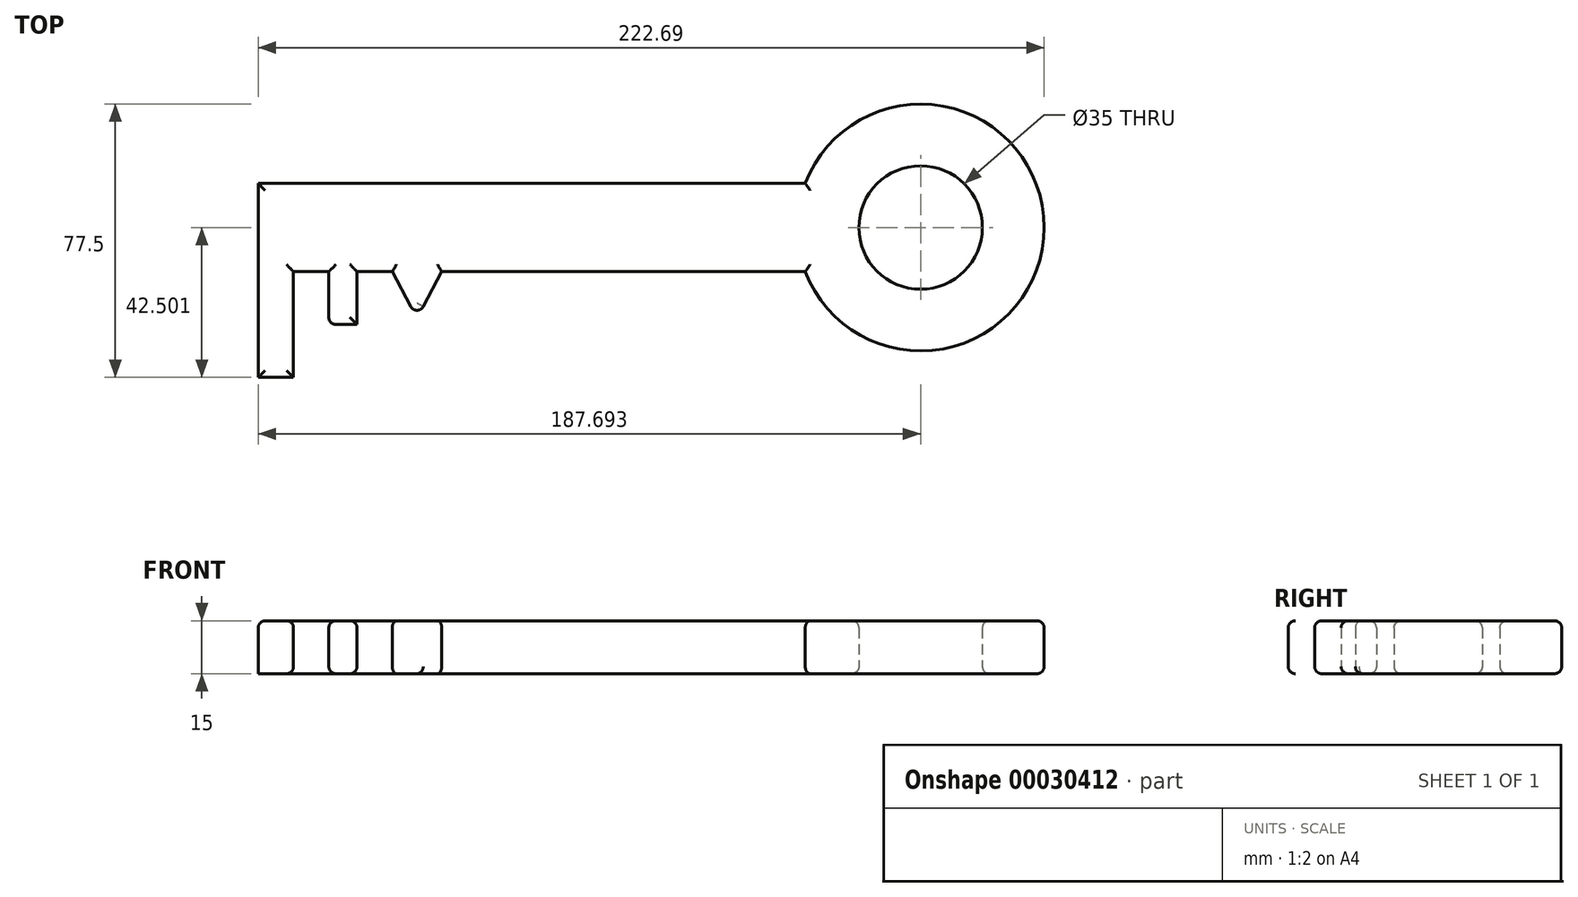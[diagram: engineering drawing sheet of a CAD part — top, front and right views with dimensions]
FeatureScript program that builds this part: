
annotation { "Feature Type Name" : "Feature", "Feature Type Description" : "" }
export const myFeature = defineFeature(function(context is Context, id is Id, definition is map)
    precondition{}
    {
        {
            var Q0;
            Q0=qCreatedBy(makeId("Top.planeOp"),FACE);
            var sketch = newSketch(context, id + "F0", { "sketchPlane" : qUnion([Q0])});
            skLineSegment(sketch, "E0.bottom", {"start": v(-9.04, 51.47) * mm, "end": v(-164.04, 51.47) * mm});
            skLineSegment(sketch, "E0.top", {"start": v(-9.04, 26.47) * mm, "end": v(-112.04, 26.47) * mm});
            skLineSegment(sketch, "E0.right", {"start": v(-164.04, 51.47) * mm, "end": v(-164.04, 26.47) * mm});
            skLineSegment(sketch, "E1.top", {"start": v(-164.04, -3.53) * mm, "end": v(-154.04, -3.53) * mm});
            skLineSegment(sketch, "E1.left", {"start": v(-164.04, 26.47) * mm, "end": v(-164.04, -3.53) * mm});
            skLineSegment(sketch, "E1.right", {"start": v(-154.04, 26.47) * mm, "end": v(-154.04, -3.53) * mm});
            skLineSegment(sketch, "E2.top", {"start": v(-144.04, 11.47) * mm, "end": v(-136.04, 11.47) * mm});
            skLineSegment(sketch, "E2.left", {"start": v(-144.04, 26.47) * mm, "end": v(-144.04, 11.47) * mm});
            skLineSegment(sketch, "E2.right", {"start": v(-136.04, 26.47) * mm, "end": v(-136.04, 11.47) * mm});
            skLineSegment(sketch, "E3", {"start": v(-126.04, 26.47) * mm, "end": v(-119.04, 13.2) * mm});
            skLineSegment(sketch, "E4", {"start": v(-119.04, 13.2) * mm, "end": v(-112.04, 26.47) * mm});
            skArc(sketch, "E5", {"start": v(-9.04, 26.47) * mm, "mid": v(58.65, 38.97) * mm, "end": v(-9.04, 51.47) * mm});
            skCircle(sketch, "E6", {"center": v(23.65, 38.97) * mm, "radius": 17.5 * mm});
            skLineSegment(sketch, "E7", {"start": v(23.65, 38.97) * mm, "end": v(-164.04, 38.97) * mm, "construction": true});
            skLineSegment(sketch, "E8.trimOffspring", {"start": v(-126.04, 26.47) * mm, "end": v(-136.04, 26.47) * mm});
            skLineSegment(sketch, "E9.trimOffspring", {"start": v(-144.04, 26.47) * mm, "end": v(-154.04, 26.47) * mm});
            skSolve(sketch);
        }
        {
            var Q0;
            Q0 = qSketchRegion(id + "F0", true);
            extrude(context, id + "F1", {"entities" : qUnion([Q0]), "depth" : 15 * mm});
        }
        {
            var Q0;
            Q0=makeQuery(id+"F1.opExtrude","CAP_EDGE",EDGE,{"disambiguationData":[OSD([sQuery(id+"F0.wireOp",EDGE,"E0.bottom")])],"isStart":false});
            var Q1;
            Q1=makeQuery(id+"F1.opExtrude","CAP_EDGE",EDGE,{"disambiguationData":[OSD([sQuery(id+"F0.wireOp",EDGE,"E0.right"),sQuery(id+"F0.wireOp",EDGE,"E1.left")])],"isStart":false});
            var Q2;
            Q2=makeQuery(id+"F1.opExtrude","CAP_EDGE",EDGE,{"disambiguationData":[OSD([sQuery(id+"F0.wireOp",EDGE,"E1.right")])],"isStart":false});
            var Q3;
            Q3=makeQuery(id+"F1.opExtrude","CAP_EDGE",EDGE,{"disambiguationData":[OSD([sQuery(id+"F0.wireOp",EDGE,"E1.top")])],"isStart":false});
            var Q4;
            Q4=makeQuery(id+"F1.opExtrude","CAP_EDGE",EDGE,{"disambiguationData":[OSD([sQuery(id+"F0.wireOp",EDGE,"E9.trimOffspring")])],"isStart":false});
            var Q5;
            Q5=makeQuery(id+"F1.opExtrude","CAP_EDGE",EDGE,{"disambiguationData":[OSD([sQuery(id+"F0.wireOp",EDGE,"E2.left")])],"isStart":false});
            var Q6;
            Q6=makeQuery(id+"F1.opExtrude","CAP_EDGE",EDGE,{"disambiguationData":[OSD([sQuery(id+"F0.wireOp",EDGE,"E2.top")])],"isStart":false});
            var Q7;
            Q7=makeQuery(id+"F1.opExtrude","CAP_EDGE",EDGE,{"disambiguationData":[OSD([sQuery(id+"F0.wireOp",EDGE,"E3")])],"isStart":false});
            var Q8;
            Q8=makeQuery(id+"F1.opExtrude","CAP_EDGE",EDGE,{"disambiguationData":[OSD([sQuery(id+"F0.wireOp",EDGE,"E8.trimOffspring")])],"isStart":false});
            var Q9;
            Q9=makeQuery(id+"F1.opExtrude","CAP_EDGE",EDGE,{"disambiguationData":[OSD([sQuery(id+"F0.wireOp",EDGE,"E2.right")])],"isStart":false});
            var Q10;
            Q10=makeQuery(id+"F1.opExtrude","CAP_EDGE",EDGE,{"disambiguationData":[OSD([sQuery(id+"F0.wireOp",EDGE,"E4")])],"isStart":false});
            var Q11;
            Q11=makeQuery(id+"F1.opExtrude","CAP_EDGE",EDGE,{"disambiguationData":[OSD([sQuery(id+"F0.wireOp",EDGE,"E0.top")])],"isStart":false});
            var Q12;
            Q12=makeQuery(id+"F1.opExtrude","CAP_EDGE",EDGE,{"disambiguationData":[OSD([sQuery(id+"F0.wireOp",EDGE,"E5")])],"isStart":false});
            var Q13;
            Q13=makeQuery(id+"F1.opExtrude","CAP_EDGE",EDGE,{"disambiguationData":[OSD([sQuery(id+"F0.wireOp",EDGE,"E6")])],"isStart":false});
            var Q14;
            Q14=makeQuery(id+"F1.opExtrude","CAP_EDGE",EDGE,{"disambiguationData":[OSD([sQuery(id+"F0.wireOp",EDGE,"E5")])],"isStart":true});
            var Q15;
            Q15=makeQuery(id+"F1.opExtrude","CAP_EDGE",EDGE,{"disambiguationData":[OSD([sQuery(id+"F0.wireOp",EDGE,"E6")])],"isStart":true});
            var Q16;
            Q16=makeQuery(id+"F1.opExtrude","CAP_EDGE",EDGE,{"disambiguationData":[OSD([sQuery(id+"F0.wireOp",EDGE,"E0.top")])],"isStart":true});
            var Q17;
            Q17=makeQuery(id+"F1.opExtrude","CAP_EDGE",EDGE,{"disambiguationData":[OSD([sQuery(id+"F0.wireOp",EDGE,"E0.bottom")])],"isStart":true});
            var Q18;
            Q18=makeQuery(id+"F1.opExtrude","CAP_EDGE",EDGE,{"disambiguationData":[OSD([sQuery(id+"F0.wireOp",EDGE,"E4")])],"isStart":true});
            var Q19;
            Q19=makeQuery(id+"F1.opExtrude","CAP_EDGE",EDGE,{"disambiguationData":[OSD([sQuery(id+"F0.wireOp",EDGE,"E8.trimOffspring")])],"isStart":true});
            var Q20;
            Q20=makeQuery(id+"F1.opExtrude","CAP_EDGE",EDGE,{"disambiguationData":[OSD([sQuery(id+"F0.wireOp",EDGE,"E2.right")])],"isStart":true});
            var Q21;
            Q21=makeQuery(id+"F1.opExtrude","CAP_EDGE",EDGE,{"disambiguationData":[OSD([sQuery(id+"F0.wireOp",EDGE,"E2.top")])],"isStart":true});
            var Q22;
            Q22=makeQuery(id+"F1.opExtrude","CAP_EDGE",EDGE,{"disambiguationData":[OSD([sQuery(id+"F0.wireOp",EDGE,"E9.trimOffspring")])],"isStart":true});
            var Q23;
            Q23=makeQuery(id+"F1.opExtrude","CAP_EDGE",EDGE,{"disambiguationData":[OSD([sQuery(id+"F0.wireOp",EDGE,"E1.right")])],"isStart":true});
            var Q24;
            Q24=makeQuery(id+"F1.opExtrude","CAP_EDGE",EDGE,{"disambiguationData":[OSD([sQuery(id+"F0.wireOp",EDGE,"E1.top")])],"isStart":true});
            fillet(context, id + "F2", {"entities" : qUnion([Q0, Q1, Q2, Q3, Q4, Q5, Q6, Q7, Q8, Q9, Q10, Q11, Q12, Q13, Q14, Q15, Q16, Q17, Q18, Q19, Q20, Q21, Q22, Q23, Q24]), "radius" : 2 * mm, "tangentPropagation" : true, "allowEdgeOverflow" : false});
        }
        {
            var Q0;
            Q0=makeQuery(id+"F1.opExtrude","CAP_EDGE",EDGE,{"disambiguationData":[OSD([sQuery(id+"F0.wireOp",EDGE,"E2.left")])],"isStart":true});
            var Q1;
            Q1=makeQuery(id+"F1.opExtrude","CAP_EDGE",EDGE,{"disambiguationData":[OSD([sQuery(id+"F0.wireOp",EDGE,"E3")])],"isStart":true});
            fillet(context, id + "F3", {"entities" : qUnion([Q0, Q1]), "radius" : 2 * mm, "tangentPropagation" : true, "allowEdgeOverflow" : false});
        }
    });
